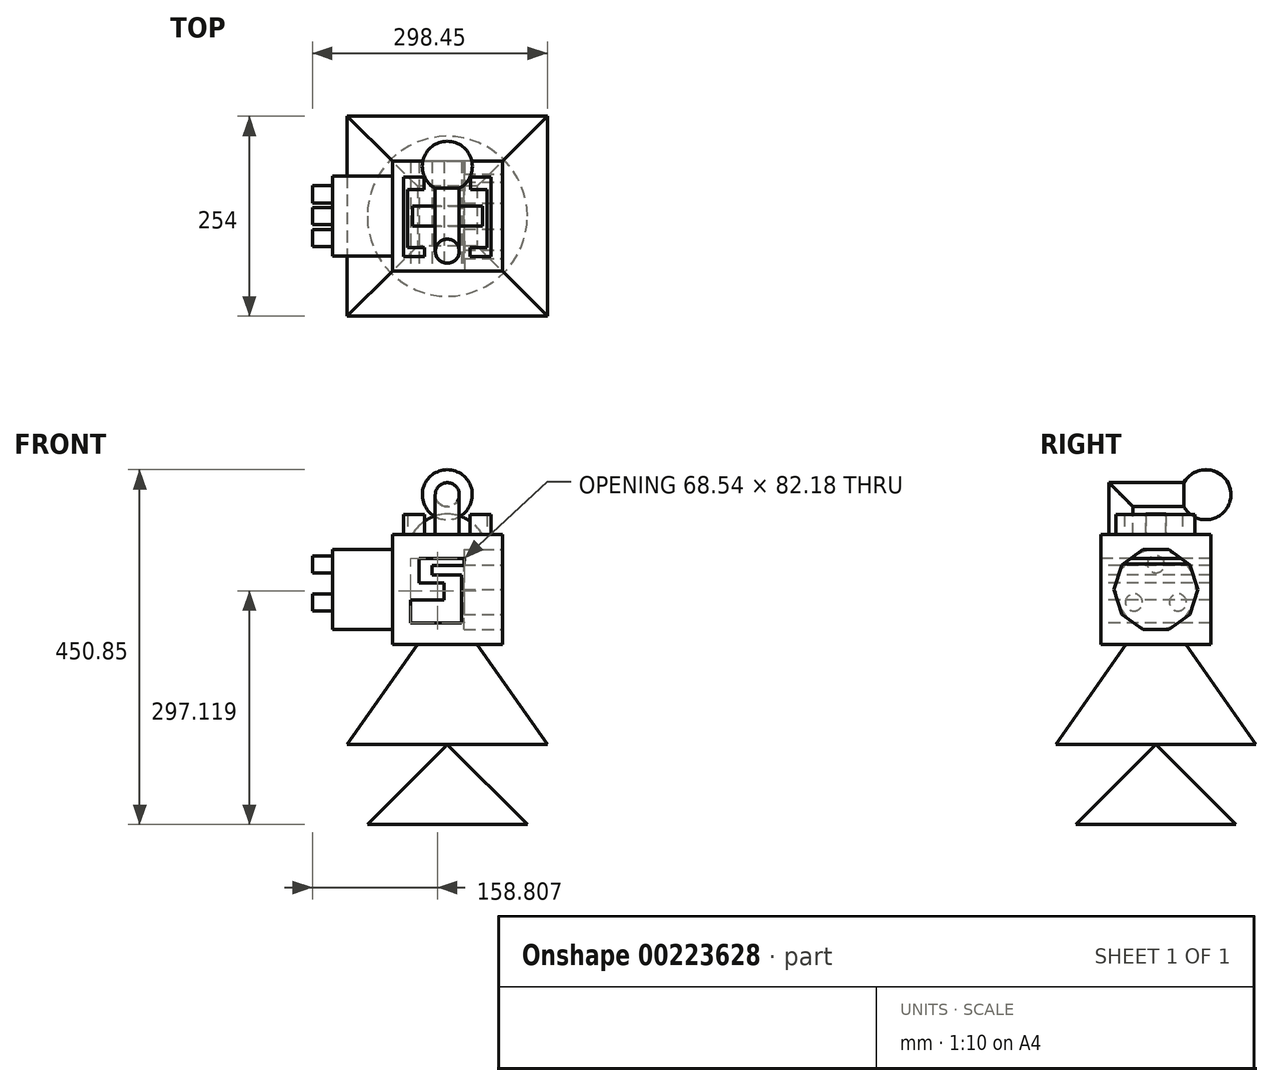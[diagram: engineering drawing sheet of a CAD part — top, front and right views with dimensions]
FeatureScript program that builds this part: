
annotation { "Feature Type Name" : "Feature", "Feature Type Description" : "" }
export const myFeature = defineFeature(function(context is Context, id is Id, definition is map)
    precondition{}
    {
        {
            var Q0;
            Q0=qCreatedBy(makeId("Front.planeOp"),FACE);
            var sketch = newSketch(context, id + "F0", { "sketchPlane" : qUnion([Q0])});
            skLineSegment(sketch, "E0.bottom", {"start": v(69.85, -69.85) * mm, "end": v(-69.85, -69.85) * mm});
            skLineSegment(sketch, "E0.top", {"start": v(69.85, 69.85) * mm, "end": v(-69.85, 69.85) * mm});
            skLineSegment(sketch, "E0.left", {"start": v(69.85, -69.85) * mm, "end": v(69.85, 69.85) * mm});
            skLineSegment(sketch, "E0.right", {"start": v(-69.85, -69.85) * mm, "end": v(-69.85, 69.85) * mm});
            skPoint(sketch, "E0.middle", {"position": v(0, 0) * mm});
            skSolve(sketch);
        }
        {
            var Q0;
            Q0 = qSketchRegion(id + "F0", true);
            extrude(context, id + "F1", {"entities" : qUnion([Q0]), "depth" : 139.7 * mm, "symmetric" : true});
        }
        {
            var Q0;
            Q0=qCreatedBy(makeId("Front.planeOp"),FACE);
            var sketch = newSketch(context, id + "F2", { "sketchPlane" : qUnion([Q0])});
            skLineSegment(sketch, "E1", {"start": v(21.63, 39.76) * mm, "end": v(-35.93, 39.76) * mm});
            skLineSegment(sketch, "E2", {"start": v(-35.93, 39.76) * mm, "end": v(-35.93, 8.82) * mm});
            skLineSegment(sketch, "E3", {"start": v(-35.93, 8.82) * mm, "end": v(-4.33, 8.82) * mm});
            skLineSegment(sketch, "E4", {"start": v(-4.33, 8.82) * mm, "end": v(-4.33, -12.8) * mm});
            skLineSegment(sketch, "E5", {"start": v(-4.33, -12.8) * mm, "end": v(-46.91, -12.8) * mm});
            skLineSegment(sketch, "E6", {"start": v(-46.91, -12.8) * mm, "end": v(-46.91, -42.42) * mm});
            skLineSegment(sketch, "E7", {"start": v(-46.91, -42.42) * mm, "end": v(18.3, -42.42) * mm});
            skLineSegment(sketch, "E8", {"start": v(18.3, -42.42) * mm, "end": v(18.3, 18.8) * mm});
            skLineSegment(sketch, "E9", {"start": v(18.3, 18.8) * mm, "end": v(-19.63, 18.8) * mm});
            skLineSegment(sketch, "E10", {"start": v(-19.63, 18.8) * mm, "end": v(-19.63, 30.78) * mm});
            skLineSegment(sketch, "E11", {"start": v(-19.63, 30.78) * mm, "end": v(20.96, 30.78) * mm});
            skLineSegment(sketch, "E12", {"start": v(20.96, 30.78) * mm, "end": v(21.63, 39.76) * mm});
            skSolve(sketch);
        }
        {
            var Q0;
            Q0 = qSketchRegion(id + "F2", true);
            extrude(context, id + "F3", {"entities" : qUnion([Q0]), "operationType" : NewBodyOperationType.REMOVE, "oppositeDirection" : true, "depth" : 139.7 * mm, "symmetric" : true});
        }
        {
            var Q0;
            Q0=qCreatedBy(makeId("Front.planeOp"),FACE);
            var sketch = newSketch(context, id + "F4", { "sketchPlane" : qUnion([Q0])});
            skArc(sketch, "E13", {"start": v(44.45, 69.85) * mm, "mid": v(0, 96.06) * mm, "end": v(-44.45, 69.85) * mm});
            skLineSegment(sketch, "E14", {"start": v(-44.45, 69.85) * mm, "end": v(44.45, 69.85) * mm});
            skSolve(sketch);
        }
        {
            var Q0;
            Q0 = qSketchRegion(id + "F4", true);
            extrude(context, id + "F5", {"entities" : qUnion([Q0]), "depth" : 25.4 * mm, "symmetric" : true});
        }
        {
            var Q0;
            Q0=makeQuery(id+"F1.opExtrude","SWEPT_FACE",FACE,{"disambiguationData":[OSD([sQuery(id+"F0.wireOp",EDGE,"E0.right")])]});
            var sketch = newSketch(context, id + "F6", { "sketchPlane" : qUnion([Q0])});
            skCircle(sketch, "E15", {"center": v(0, 0) * mm, "radius": 50.8 * mm});
            skSolve(sketch);
        }
        {
            var Q0;
            Q0 = qSketchRegion(id + "F6", true);
            extrude(context, id + "F7", {"entities" : qUnion([Q0]), "operationType" : NewBodyOperationType.ADD, "depth" : 76.2 * mm});
        }
        {
            var Q0;
            Q0=makeQuery(id+"F1.opExtrude","SWEPT_FACE",FACE,{"disambiguationData":[OSD([sQuery(id+"F0.wireOp",EDGE,"E0.left")])]});
            var sketch = newSketch(context, id + "F8", { "sketchPlane" : qUnion([Q0])});
            skCircle(sketch, "E16.cCircle", {"center": v(0, 0) * mm, "radius": 50.8 * mm, "construction": true});
            skLineSegment(sketch, "E16.0", {"start": v(43.21, -31.4) * mm, "end": v(16.5, -50.8) * mm});
            skLineSegment(sketch, "E16.1", {"start": v(16.5, -50.8) * mm, "end": v(-16.5, -50.8) * mm});
            skLineSegment(sketch, "E16.2", {"start": v(-16.5, -50.8) * mm, "end": v(-43.21, -31.4) * mm});
            skLineSegment(sketch, "E16.3", {"start": v(-43.21, -31.4) * mm, "end": v(-53.41, 0) * mm});
            skLineSegment(sketch, "E16.4", {"start": v(-53.41, 0) * mm, "end": v(-43.21, 31.4) * mm});
            skLineSegment(sketch, "E16.5", {"start": v(-43.21, 31.4) * mm, "end": v(-16.5, 50.8) * mm});
            skLineSegment(sketch, "E16.6", {"start": v(-16.5, 50.8) * mm, "end": v(16.5, 50.8) * mm});
            skLineSegment(sketch, "E16.7", {"start": v(16.5, 50.8) * mm, "end": v(43.21, 31.4) * mm});
            skLineSegment(sketch, "E16.8", {"start": v(43.21, 31.4) * mm, "end": v(53.41, 0) * mm});
            skLineSegment(sketch, "E16.9", {"start": v(53.41, 0) * mm, "end": v(43.21, -31.4) * mm});
            skPoint(sketch, "E16.0.midPoint", {"position": v(29.86, -41.1) * mm});
            skSolve(sketch);
        }
        {
            var Q0;
            Q0 = qSketchRegion(id + "F8", true);
            extrude(context, id + "F9", {"entities" : qUnion([Q0]), "operationType" : NewBodyOperationType.REMOVE, "oppositeDirection" : true, "depth" : 48.77 * mm});
        }
        {
            var Q0;
            Q0=makeQuery(id+"F1.opExtrude","SWEPT_FACE",FACE,{"disambiguationData":[OSD([sQuery(id+"F0.wireOp",EDGE,"E0.top")])]});
            var sketch = newSketch(context, id + "F10", { "sketchPlane" : qUnion([Q0])});
            skCircle(sketch, "E17", {"center": v(0, -44.45) * mm, "radius": 15.24 * mm});
            skSolve(sketch);
        }
        {
            var Q0;
            Q0=qCreatedBy(makeId("Right.planeOp"),FACE);
            var sketch = newSketch(context, id + "F11", { "sketchPlane" : qUnion([Q0])});
            skLineSegment(sketch, "E18", {"start": v(-44.45, 69.98) * mm, "end": v(-44.45, 120.78) * mm});
            skLineSegment(sketch, "E19", {"start": v(-44.45, 120.78) * mm, "end": v(44.45, 120.78) * mm});
            skLineSegment(sketch, "E20", {"start": v(44.45, 120.78) * mm, "end": v(44.45, 69.85) * mm});
            skSolve(sketch);
        }
        {
            var Q0;
            Q0=makeQuery(id+"F10.imprint","IMPRINT",FACE,{"disambiguationData":[TD([[makeQuery(id+"F10.imprint","IMPRINT",EDGE,{"derivedFrom":sQuery(id+"F10.wireOp",EDGE,"E17")}),1.0]])]});
            var Q1;
            Q1=sQuery(id+"F11.wireOp",EDGE,"E18");
            var Q2;
            Q2=sQuery(id+"F11.wireOp",EDGE,"E19");
            sweep(context, id + "F12", {"operationType" : NewBodyOperationType.ADD, "profiles" : qUnion([Q0]), "path" : qUnion([Q1, Q2])});
        }
        {
            var Q0;
            Q0=makeQuery(id+"F1.opExtrude","SWEPT_FACE",FACE,{"disambiguationData":[OSD([sQuery(id+"F0.wireOp",EDGE,"E0.bottom")])]});
            var sketch = newSketch(context, id + "F13", { "sketchPlane" : qUnion([Q0])});
            skLineSegment(sketch, "E21.bottom", {"start": v(38.1, -38.1) * mm, "end": v(-38.1, -38.1) * mm});
            skLineSegment(sketch, "E21.top", {"start": v(38.1, 38.1) * mm, "end": v(-38.1, 38.1) * mm});
            skLineSegment(sketch, "E21.left", {"start": v(38.1, -38.1) * mm, "end": v(38.1, 38.1) * mm});
            skLineSegment(sketch, "E21.right", {"start": v(-38.1, -38.1) * mm, "end": v(-38.1, 38.1) * mm});
            skPoint(sketch, "E21.middle", {"position": v(0, 0) * mm});
            skSolve(sketch);
        }
        {
            var Q0;
            Q0=makeQuery(id+"F13.imprint","IMPRINT",FACE,{"disambiguationData":[TD([[makeQuery(id+"F13.imprint","IMPRINT",EDGE,{"derivedFrom":sQuery(id+"F13.wireOp",EDGE,"E21.bottom")}),1.0]])]});
            cPlane(context, id + "F14", {"entities" : qUnion([Q0]), "cplaneType" : CPlaneType.OFFSET, "offset" : 127 * mm, "width" : 152.4 * mm, "height" : 152.4 * mm});
        }
        {
            var Q0;
            Q0=qCreatedBy(id+"F14.planeOp",FACE);
            var sketch = newSketch(context, id + "F15", { "sketchPlane" : qUnion([Q0])});
            skLineSegment(sketch, "E22.bottom", {"start": v(127, -127) * mm, "end": v(-127, -127) * mm});
            skLineSegment(sketch, "E22.top", {"start": v(127, 127) * mm, "end": v(-127, 127) * mm});
            skLineSegment(sketch, "E22.left", {"start": v(127, -127) * mm, "end": v(127, 127) * mm});
            skLineSegment(sketch, "E22.right", {"start": v(-127, -127) * mm, "end": v(-127, 127) * mm});
            skPoint(sketch, "E22.middle", {"position": v(0, 0) * mm});
            skSolve(sketch);
        }
        {
            var Q1;
            Q1=makeQuery(id+"F13.imprint","IMPRINT",FACE,{"disambiguationData":[TD([[makeQuery(id+"F13.imprint","IMPRINT",EDGE,{"derivedFrom":sQuery(id+"F13.wireOp",EDGE,"E21.bottom")}),-1.0]])]});
            var Q2;
            Q2=makeQuery(id+"F15.imprint","IMPRINT",FACE,{"disambiguationData":[TD([[makeQuery(id+"F15.imprint","IMPRINT",EDGE,{"derivedFrom":sQuery(id+"F15.wireOp",EDGE,"E22.bottom")}),-1.0]])]});
            loft(context, id + "F16", {"operationType" : NewBodyOperationType.ADD, "sheetProfilesArray" : [{ "sheetProfileEntities" : qUnion([Q1]) }, { "sheetProfileEntities" : qUnion([Q2]) }]});
        }
        {
            var Q0;
            Q0=qCreatedBy(makeId("Right.planeOp"),FACE);
            var sketch = newSketch(context, id + "F17", { "sketchPlane" : qUnion([Q0])});
            skLineSegment(sketch, "E23", {"start": v(31.75, 120.65) * mm, "end": v(95.25, 120.65) * mm});
            skArc(sketch, "E24", {"start": v(95.25, 120.65) * mm, "mid": v(63.5, 152.4) * mm, "end": v(31.75, 120.65) * mm});
            skSolve(sketch);
        }
        {
            var Q0;
            Q0 = qSketchRegion(id + "F17", true);
            var Q1;
            Q1=sQuery(id+"F17.wireOp",EDGE,"E23");
            revolve(context, id + "F18", {"operationType" : NewBodyOperationType.ADD, "entities" : qUnion([Q0]), "axis" : qUnion([Q1]), "revolveType" : RevolveType.FULL});
        }
        {
            var Q0;
            Q0=qCreatedBy(makeId("Front.planeOp"),FACE);
            var sketch = newSketch(context, id + "F19", { "sketchPlane" : qUnion([Q0])});
            skLineSegment(sketch, "E25", {"start": v(0, -196.85) * mm, "end": v(0, -298.45) * mm});
            skLineSegment(sketch, "E26", {"start": v(0, -298.45) * mm, "end": v(-101.6, -298.45) * mm});
            skLineSegment(sketch, "E27", {"start": v(-101.6, -298.45) * mm, "end": v(0, -196.85) * mm});
            skSolve(sketch);
        }
        {
            var Q0;
            Q0=makeQuery(id+"F19.imprint","IMPRINT",FACE,{"disambiguationData":[TD([[makeQuery(id+"F19.imprint","IMPRINT",EDGE,{"derivedFrom":sQuery(id+"F19.wireOp",EDGE,"E25")}),-1.0]])]});
            var Q1;
            Q1=sQuery(id+"F19.wireOp",EDGE,"E25");
            revolve(context, id + "F20", {"entities" : qUnion([Q0]), "axis" : qUnion([Q1]), "revolveType" : RevolveType.FULL});
        }
        {
            var Q0;
            Q0=makeQuery(id+"F1.opExtrude","SWEPT_FACE",FACE,{"disambiguationData":[OSD([sQuery(id+"F0.wireOp",EDGE,"E0.top")])]});
            var sketch = newSketch(context, id + "F21", { "sketchPlane" : qUnion([Q0])});
            skLineSegment(sketch, "E28", {"start": v(-55.69, 49.73) * mm, "end": v(-55.69, -51.15) * mm});
            skLineSegment(sketch, "E29", {"start": v(-55.69, -51.15) * mm, "end": v(-29.05, -51.15) * mm});
            skLineSegment(sketch, "E30", {"start": v(-29.05, -51.15) * mm, "end": v(-29.05, -39.82) * mm});
            skLineSegment(sketch, "E31", {"start": v(-29.05, -39.82) * mm, "end": v(-50.49, -39.82) * mm});
            skLineSegment(sketch, "E32", {"start": v(-50.49, -39.82) * mm, "end": v(-50.49, 33.86) * mm});
            skLineSegment(sketch, "E33", {"start": v(-50.49, 33.86) * mm, "end": v(-29.52, 33.86) * mm});
            skLineSegment(sketch, "E34", {"start": v(-29.52, 33.86) * mm, "end": v(-29.52, 49.73) * mm});
            skLineSegment(sketch, "E35", {"start": v(-29.52, 49.73) * mm, "end": v(-55.69, 49.73) * mm});
            skLineSegment(sketch, "E36", {"start": v(0, 0) * mm, "end": v(0, 160.25) * mm, "construction": true});
            skLineSegment(sketch, "E37.MirrorCS", {"start": v(50.49, 33.86) * mm, "end": v(29.52, 33.86) * mm});
            skLineSegment(sketch, "E38.MirrorCS", {"start": v(29.52, 33.86) * mm, "end": v(29.52, 49.73) * mm});
            skLineSegment(sketch, "E39.MirrorCS", {"start": v(29.52, 49.73) * mm, "end": v(55.69, 49.73) * mm});
            skLineSegment(sketch, "E40.MirrorCS", {"start": v(55.69, 49.73) * mm, "end": v(55.69, -51.15) * mm});
            skLineSegment(sketch, "E41.MirrorCS", {"start": v(55.69, -51.15) * mm, "end": v(29.05, -51.15) * mm});
            skLineSegment(sketch, "E42.MirrorCS", {"start": v(29.05, -39.82) * mm, "end": v(50.49, -39.82) * mm});
            skLineSegment(sketch, "E43.MirrorCS", {"start": v(50.49, -39.82) * mm, "end": v(50.49, 33.86) * mm});
            skLineSegment(sketch, "E44.MirrorCS", {"start": v(29.05, -51.15) * mm, "end": v(29.05, -39.82) * mm});
            skSolve(sketch);
        }
        {
            var Q0;
            Q0 = qSketchRegion(id + "F21", true);
            extrude(context, id + "F22", {"entities" : qUnion([Q0]), "operationType" : NewBodyOperationType.ADD, "depth" : 25.4 * mm});
        }
        {
            var Q0;
            Q0=makeQuery(id+"F7.opExtrude","CAP_FACE",FACE,{"disambiguationData":[OSD([sQuery(id+"F6.wireOp",EDGE,"E15")])],"isStart":false});
            var sketch = newSketch(context, id + "F23", { "sketchPlane" : qUnion([Q0])});
            skCircle(sketch, "E45", {"center": v(0, 0) * mm, "radius": 32.23 * mm, "construction": true});
            skCircle(sketch, "E46", {"center": v(0, 32.23) * mm, "radius": 10.85 * mm});
            skCircle(sketch, "E47.1.1", {"center": v(-27.91, -16.12) * mm, "radius": 10.85 * mm});
            skCircle(sketch, "E47.2.1", {"center": v(27.91, -16.12) * mm, "radius": 10.85 * mm});
            skSolve(sketch);
        }
        {
            var Q0;
            Q0 = qSketchRegion(id + "F23", true);
            extrude(context, id + "F24", {"entities" : qUnion([Q0]), "operationType" : NewBodyOperationType.ADD, "depth" : 25.4 * mm});
        }
    });
